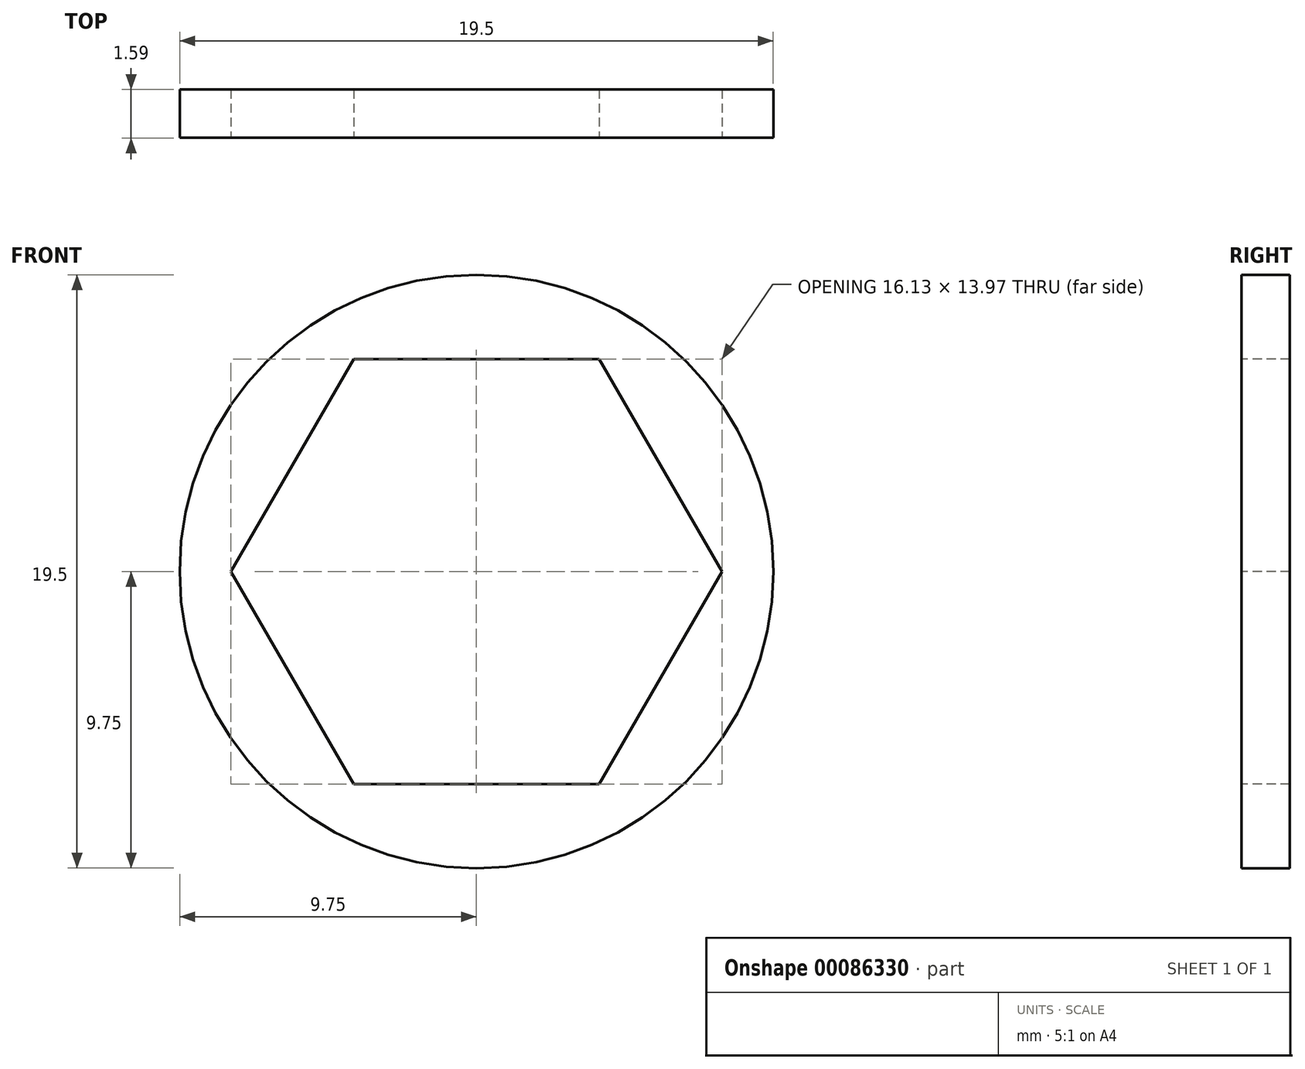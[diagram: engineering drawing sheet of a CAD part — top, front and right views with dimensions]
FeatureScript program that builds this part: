
annotation { "Feature Type Name" : "Feature", "Feature Type Description" : "" }
export const myFeature = defineFeature(function(context is Context, id is Id, definition is map)
    precondition{}
    {
        {
            var Q0;
            Q0=qCreatedBy(makeId("Front.planeOp"),FACE);
            var sketch = newSketch(context, id + "F0", { "sketchPlane" : qUnion([Q0])});
            skCircle(sketch, "E0", {"center": v(0, 0) * mm, "radius": 9.75 * mm});
            skSolve(sketch);
        }
        {
            var Q0;
            Q0 = qSketchRegion(id + "F0", true);
            extrude(context, id + "F1", {"entities" : qUnion([Q0]), "depth" : 1.59 * mm});
        }
        {
            var Q0;
            Q0=makeQuery(id+"F1.opExtrude","CAP_FACE",FACE,{"disambiguationData":[OSD([sQuery(id+"F0.wireOp",EDGE,"E0")])],"isStart":false});
            var sketch = newSketch(context, id + "F2", { "sketchPlane" : qUnion([Q0])});
            skCircle(sketch, "E1.cCircle", {"center": v(0, 0) * mm, "radius": 8.07 * mm, "construction": true});
            skLineSegment(sketch, "E1.0", {"start": v(8.07, 0) * mm, "end": v(4.03, -6.99) * mm});
            skLineSegment(sketch, "E1.1", {"start": v(4.03, -6.99) * mm, "end": v(-4.03, -6.99) * mm});
            skLineSegment(sketch, "E1.2", {"start": v(-4.03, -6.99) * mm, "end": v(-8.07, 0) * mm});
            skLineSegment(sketch, "E1.3", {"start": v(-8.07, 0) * mm, "end": v(-4.03, 6.99) * mm});
            skLineSegment(sketch, "E1.4", {"start": v(-4.03, 6.99) * mm, "end": v(4.03, 6.99) * mm});
            skLineSegment(sketch, "E1.5", {"start": v(4.03, 6.99) * mm, "end": v(8.07, 0) * mm});
            skSolve(sketch);
        }
        {
            var Q0;
            Q0 = qSketchRegion(id + "F2", true);
            extrude(context, id + "F3", {"entities" : qUnion([Q0]), "operationType" : NewBodyOperationType.REMOVE, "endBound" : BoundingType.THROUGH_ALL, "oppositeDirection" : true, "depth" : 25.4 * mm});
        }
    });
